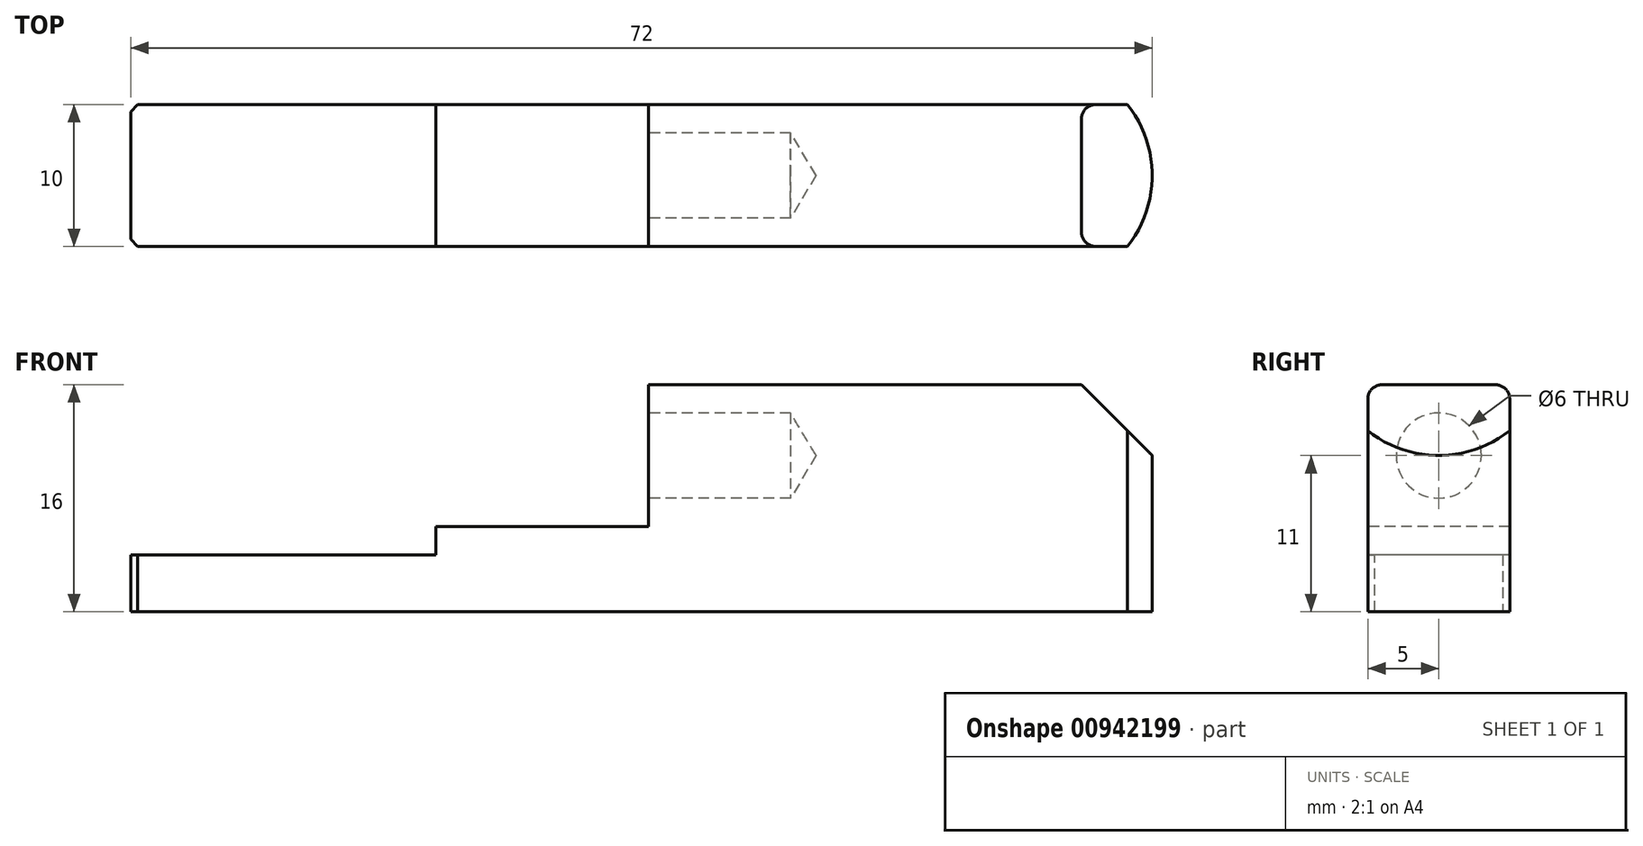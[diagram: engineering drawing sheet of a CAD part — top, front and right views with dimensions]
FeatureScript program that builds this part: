
annotation { "Feature Type Name" : "Feature", "Feature Type Description" : "" }
export const myFeature = defineFeature(function(context is Context, id is Id, definition is map)
    precondition{}
    {
        {
            var Q0;
            Q0=qCreatedBy(makeId("Top.planeOp"),FACE);
            var sketch = newSketch(context, id + "F0", { "sketchPlane" : qUnion([Q0])});
            skLineSegment(sketch, "E0.bottom", {"start": v(36, -5) * mm, "end": v(-36, -5) * mm});
            skLineSegment(sketch, "E0.top", {"start": v(36, 5) * mm, "end": v(-36, 5) * mm});
            skLineSegment(sketch, "E0.left", {"start": v(36, -5) * mm, "end": v(36, 5) * mm});
            skLineSegment(sketch, "E0.right", {"start": v(-36, -5) * mm, "end": v(-36, 5) * mm});
            skPoint(sketch, "E0.middle", {"position": v(0, 0) * mm});
            skSolve(sketch);
        }
        {
            var Q0;
            Q0 = qSketchRegion(id + "F0", true);
            extrude(context, id + "F1", {"entities" : qUnion([Q0]), "depth" : 16 * mm, "offsetDistance" : 25 * mm});
        }
        {
            var Q0;
            Q0=makeQuery(id+"F1.opExtrude","SWEPT_FACE",FACE,{"disambiguationData":[OSD([sQuery(id+"F0.wireOp",EDGE,"E0.bottom")])]});
            var sketch = newSketch(context, id + "F2", { "sketchPlane" : qUnion([Q0])});
            skLineSegment(sketch, "E1", {"start": v(-36, 4) * mm, "end": v(-36, 16) * mm});
            skLineSegment(sketch, "E2", {"start": v(-36, 16) * mm, "end": v(0.5, 16) * mm});
            skLineSegment(sketch, "E3", {"start": v(0.5, 16) * mm, "end": v(0.5, 6) * mm});
            skLineSegment(sketch, "E4", {"start": v(0.5, 6) * mm, "end": v(-14.5, 6) * mm});
            skLineSegment(sketch, "E5", {"start": v(-14.5, 6) * mm, "end": v(-14.5, 4) * mm});
            skLineSegment(sketch, "E6", {"start": v(-14.5, 4) * mm, "end": v(-36, 4) * mm});
            skSolve(sketch);
        }
        {
            var Q0;
            Q0 = qSketchRegion(id + "F2", true);
            extrude(context, id + "F3", {"entities" : qUnion([Q0]), "operationType" : NewBodyOperationType.REMOVE, "oppositeDirection" : true, "depth" : 25 * mm, "offsetDistance" : 25 * mm});
        }
        {
            var Q0;
            Q0=makeQuery(id+"F3.boolean.opBoolean","COPY",FACE,{"derivedFrom":makeQuery(id+"F3.opExtrude","SWEPT_FACE",FACE,{"disambiguationData":[OSD([sQuery(id+"F2.wireOp",EDGE,"E3")])]})});
            var sketch = newSketch(context, id + "F4", { "sketchPlane" : qUnion([Q0])});
            skPoint(sketch, "E7", {"position": v(0, 11) * mm});
            skSolve(sketch);
        }
        {
            var Q0;
            Q0=sQuery(id+"F4.wireOp",VERTEX,"E7");
            var Q1;
            Q1=makeQuery(id+"F1.opExtrude","SWEPT_BODY",BODY,{"disambiguationData":[OSD([sQuery(id+"F0.wireOp",EDGE,"E0.bottom"),sQuery(id+"F0.wireOp",EDGE,"E0.top"),sQuery(id+"F0.wireOp",EDGE,"E0.left"),sQuery(id+"F0.wireOp",EDGE,"E0.right")])]});
            hole(context, id + "F5", {"style" : HoleStyle.SIMPLE, "endStyle" : HoleEndStyle.BLIND, "holeDiameter" : 6 * mm, "majorDiameter" : 5 * mm, "holeDepth" : 10 * mm, "isTappedThrough" : true, "tappedDepth" : 8.5 * mm, "tapClearance" : 3, "startFromSketch" : true, "locations" : qUnion([Q0]), "scope" : qUnion([Q1])});
        }
        {
            var Q0;
            Q0=makeQuery(id+"F3.boolean.opBoolean","COPY",EDGE,{"derivedFrom":makeQuery(id+"F3.opExtrude","SWEPT_EDGE",EDGE,{"disambiguationData":[OSD([sQuery(id+"F0.wireOp",EDGE,"E0.bottom"),sQuery(id+"F0.wireOp",EDGE,"E0.right"),sQuery(id+"F2.wireOp",EDGE,"E1"),sQuery(id+"F2.wireOp",EDGE,"E6")])]})});
            var Q1;
            Q1=makeQuery(id+"F1.opExtrude","SWEPT_EDGE",EDGE,{"disambiguationData":[OSD([sQuery(id+"F0.wireOp",EDGE,"E0.bottom"),sQuery(id+"F0.wireOp",EDGE,"E0.right")])]});
            var Q2;
            Q2=makeQuery(id+"F1.opExtrude","SWEPT_EDGE",EDGE,{"disambiguationData":[OSD([sQuery(id+"F0.wireOp",EDGE,"E0.top"),sQuery(id+"F0.wireOp",EDGE,"E0.right")])]});
            chamfer(context, id + "F6", {"entities" : qUnion([Q0, Q1, Q2]), "width" : 0.5 * mm, "tangentPropagation" : true});
        }
        {
            var Q0;
            Q0=makeQuery(id+"F1.opExtrude","CAP_EDGE",EDGE,{"disambiguationData":[OSD([sQuery(id+"F0.wireOp",EDGE,"E0.left")])],"isStart":false});
            chamfer(context, id + "F7", {"entities" : qUnion([Q0]), "width" : 5 * mm, "tangentPropagation" : true});
        }
        {
            var Q0;
            Q0=makeQuery(id+"F1.opExtrude","CAP_EDGE",EDGE,{"disambiguationData":[OSD([sQuery(id+"F0.wireOp",EDGE,"E0.bottom")])],"isStart":false});
            var Q1;
            Q1=makeQuery(id+"F1.opExtrude","CAP_EDGE",EDGE,{"disambiguationData":[OSD([sQuery(id+"F0.wireOp",EDGE,"E0.top")])],"isStart":false});
            fillet(context, id + "F8", {"entities" : qUnion([Q0, Q1]), "radius" : 1 * mm, "tangentPropagation" : true, "allowEdgeOverflow" : false});
        }
        {
            var Q0;
            Q0=qCreatedBy(makeId("Top.planeOp"),FACE);
            var sketch = newSketch(context, id + "F9", { "sketchPlane" : qUnion([Q0])});
            skArc(sketch, "E8", {"start": v(34.24, -5) * mm, "mid": v(36, 0) * mm, "end": v(34.24, 5) * mm});
            skPoint(sketch, "E9", {"position": v(36, 0) * mm});
            skLineSegment(sketch, "E10", {"start": v(34.24, 5) * mm, "end": v(37.15, 5) * mm});
            skLineSegment(sketch, "E11", {"start": v(37.15, 5) * mm, "end": v(37.15, -5) * mm});
            skLineSegment(sketch, "E12", {"start": v(37.15, -5) * mm, "end": v(34.24, -5) * mm});
            skSolve(sketch);
        }
        {
            var Q0;
            Q0=makeQuery(id+"F9.imprint","IMPRINT",FACE,{"disambiguationData":[TD([[makeQuery(id+"F9.imprint","IMPRINT",EDGE,{"derivedFrom":sQuery(id+"F9.wireOp",EDGE,"E8")}),-1.0]])]});
            extrude(context, id + "F10", {"entities" : qUnion([Q0]), "operationType" : NewBodyOperationType.REMOVE, "depth" : 20 * mm, "offsetDistance" : 25 * mm});
        }
    });
